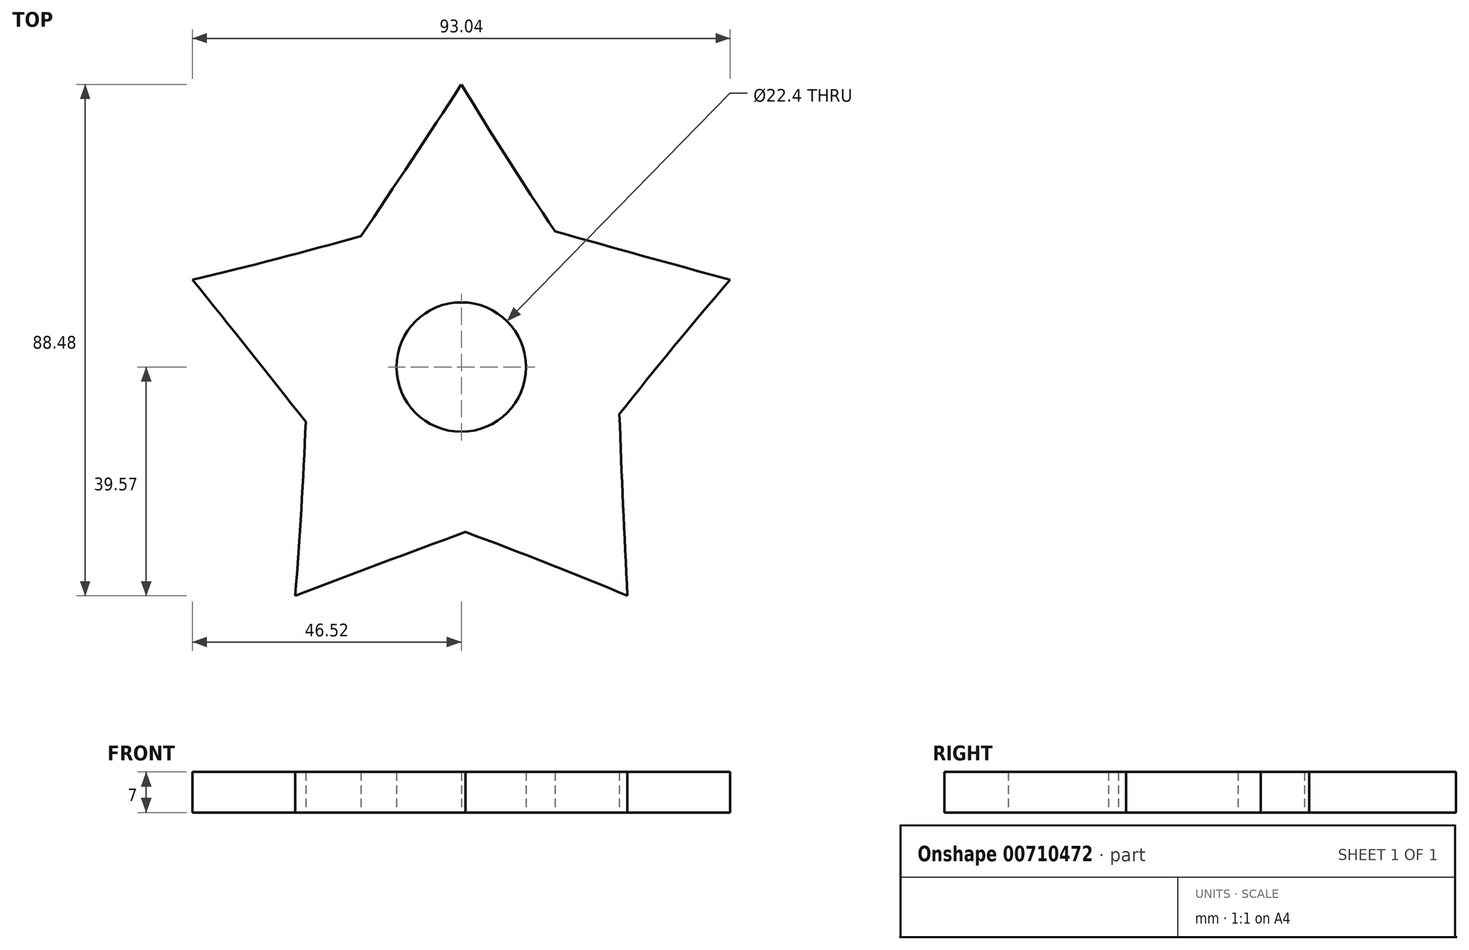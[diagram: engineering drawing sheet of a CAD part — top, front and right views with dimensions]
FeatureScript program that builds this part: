
annotation { "Feature Type Name" : "Feature", "Feature Type Description" : "" }
export const myFeature = defineFeature(function(context is Context, id is Id, definition is map)
    precondition{}
    {
        {
            var Q0;
            Q0=qCreatedBy(makeId("Top.planeOp"),FACE);
            var sketch = newSketch(context, id + "F0", { "sketchPlane" : qUnion([Q0])});
            skCircle(sketch, "E0", {"center": v(0, 0) * mm, "radius": 11.2 * mm});
            skArc(sketch, "E1", {"start": v(-17.34, 22.68) * mm, "mid": v(-8.62, 35.76) * mm, "end": v(0, 48.9) * mm});
            skArc(sketch, "E2", {"start": v(0, 48.9) * mm, "mid": v(7.97, 36.12) * mm, "end": v(16.2, 23.5) * mm});
            skArc(sketch, "E3.1.0", {"start": v(-26.93, -9.49) * mm, "mid": v(-36.67, 2.85) * mm, "end": v(-46.52, 15.11) * mm});
            skArc(sketch, "E3.1.1", {"start": v(-46.52, 15.11) * mm, "mid": v(-31.89, 18.74) * mm, "end": v(-17.34, 22.68) * mm});
            skArc(sketch, "E3.2.0", {"start": v(0.7, -28.54) * mm, "mid": v(-14.04, -34) * mm, "end": v(-28.75, -39.57) * mm});
            skArc(sketch, "E3.2.1", {"start": v(-28.75, -39.57) * mm, "mid": v(-27.68, -24.54) * mm, "end": v(-26.93, -9.49) * mm});
            skArc(sketch, "E4.3.3.0", {"start": v(27.36, -8.15) * mm, "mid": v(28, -23.86) * mm, "end": v(28.75, -39.57) * mm});
            skArc(sketch, "E4.4.3.0", {"start": v(28.75, -39.57) * mm, "mid": v(14.78, -33.9) * mm, "end": v(0.7, -28.54) * mm});
            skArc(sketch, "E4.3.4.0", {"start": v(16.2, 23.5) * mm, "mid": v(31.35, 19.25) * mm, "end": v(46.52, 15.11) * mm});
            skArc(sketch, "E4.4.4.0", {"start": v(46.52, 15.11) * mm, "mid": v(36.81, 3.58) * mm, "end": v(27.36, -8.15) * mm});
            skPoint(sketch, "E5.orphan", {"position": v(-4.28, 26.5) * mm});
            skPoint(sketch, "E6.orphan", {"position": v(-24.4, 12.26) * mm});
            skPoint(sketch, "E7.end.orphan", {"position": v(-69.3, 12.26) * mm});
            skPoint(sketch, "E8.orphan", {"position": v(4.12, 26.98) * mm});
            skPoint(sketch, "E9.orphan", {"position": v(23.87, 12.26) * mm});
            skPoint(sketch, "E10.orphan", {"position": v(26.94, 4.42) * mm});
            skPoint(sketch, "E11.orphan", {"position": v(19.04, -18.92) * mm});
            skPoint(sketch, "E12.orphan", {"position": v(12.53, -24.25) * mm});
            skPoint(sketch, "E13.orphan", {"position": v(-12.1, -23.95) * mm});
            skPoint(sketch, "E14.orphan", {"position": v(-19.2, -19.4) * mm});
            skPoint(sketch, "E15.orphan", {"position": v(-26.52, 4.11) * mm});
            skSolve(sketch);
        }
        {
            var Q0;
            Q0=makeQuery(id+"F0.imprint","IMPRINT",FACE,{"disambiguationData":[TD([[makeQuery(id+"F0.imprint","IMPRINT",EDGE,{"derivedFrom":sQuery(id+"F0.wireOp",EDGE,"E1")}),-1.0]])]});
            extrude(context, id + "F1", {"entities" : qUnion([Q0]), "depth" : 7 * mm, "offsetDistance" : 25 * mm});
        }
    });
